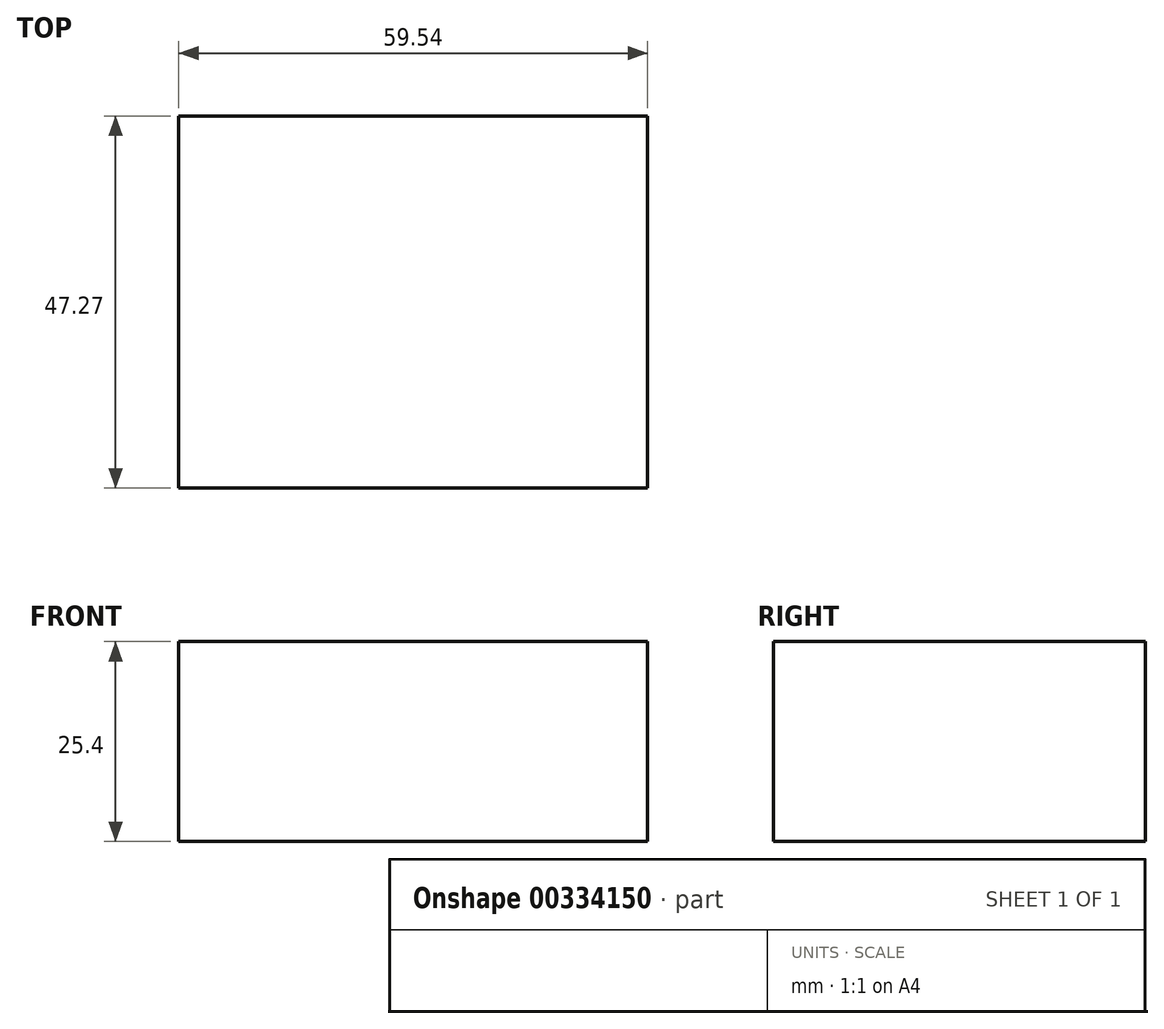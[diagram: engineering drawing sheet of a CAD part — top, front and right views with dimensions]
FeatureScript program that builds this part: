
annotation { "Feature Type Name" : "Feature", "Feature Type Description" : "" }
export const myFeature = defineFeature(function(context is Context, id is Id, definition is map)
    precondition{}
    {
        {
            var Q0;
            Q0=qCreatedBy(makeId("Top.planeOp"),FACE);
            var sketch = newSketch(context, id + "F0", { "sketchPlane" : qUnion([Q0])});
            skLineSegment(sketch, "E0.bottom", {"start": v(59.54, 47.27) * mm, "end": v(0, 47.27) * mm});
            skLineSegment(sketch, "E0.top", {"start": v(59.54, 0) * mm, "end": v(0, 0) * mm});
            skLineSegment(sketch, "E0.left", {"start": v(59.54, 47.27) * mm, "end": v(59.54, 0) * mm});
            skLineSegment(sketch, "E0.right", {"start": v(0, 47.27) * mm, "end": v(0, 0) * mm});
            skSolve(sketch);
        }
        {
            var Q0;
            Q0=makeQuery(id+"F0.imprint","IMPRINT",FACE,{"disambiguationData":[TD([[makeQuery(id+"F0.imprint","IMPRINT",EDGE,{"derivedFrom":sQuery(id+"F0.wireOp",EDGE,"E0.bottom")}),1.0]])]});
            extrude(context, id + "F1", {"entities" : qUnion([Q0]), "depth" : 25.4 * mm});
        }
    });
